# Revit family: Wall_Cabinets-Teknion-RHWP_Pigeonhole_Wall_Cabinet-R2018
name_source: partatom
category: Furniture
revit_build: Autodesk Revit 2018 (Build: 20190510_1515(x64)
units: mm (PartAtom-declared; Revit-internal decimal feet)

## family parameters
Always vertical = Yes
Cut with Voids When Loaded = No
OmniClass Number = 23.40.20.00
OmniClass Title = General Furniture and Specialties
Room Calculation Point = No
Shared = Yes
Work Plane-Based = No

## types (3) — shared parameters
Assembly Code = E2020200
Case Finish = Source Laminate - Teknion - 3M - Provincial Oak
For Additional Finishes please visit = https://assets.teknion.com
Manufacturer = Teknion
Manufacturer Fax = 416.661.4586
Part Number = RHWP
Product Documentation Link = https://www.teknion.com
Product Line = Modular Cabinets
Product Page URL = https://www.teknion.com
Series = Modular Cabinets
Sustainability Data = https://www.teknion.com
To render please download texture images found here = https://assets.teknion.com
URL = www.teknion.com
Unit Weight URL = http://www.teknion.com
Warranty = http://www.teknion.com

## per-type parameters (varying)
| type | Description | Horizontal Shelf | Material Note | Model | Shelf Finish |
| Laminate Horizontal | Pigeonhole Wall Cabinet, Laminate Horizontal Divider Direction, 15" Depth | Yes | Shelf Finish must match Case Finish | RHWPH15____ | Source Laminate - Teknion - 3M - Provincial Oak |
| Metal Horizontal | Pigeonhole Wall Cabinet, Metal Horizontal Divider Direction, 15" Depth | Yes | Shelf Finish must be Metal Finish coordinated with Case Finish | RHWPM15____ | Paint - Teknion - Mica - Sepia Bronze |
| Laminate Vertical | Pigeonhole Wall Cabinet, Laminate Vertical Divider Direction, 15" Depth | No | Shelf Finish must match Case Finish | RHWPV15____ | Source Laminate - Teknion - 3M - Provincial Oak |

type visibility flags (boolean, named after types; folded from table):
- Laminate Horizontal: Yes: Laminate Horizontal
- Metal Horizontal: Yes: (none)
- Laminate Vertical: Yes: Laminate Vertical

## geometry (parser evidence)
native form markers: Sweep x2
no freeform markers — native parametric forms only
